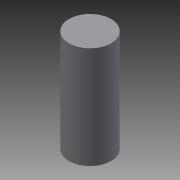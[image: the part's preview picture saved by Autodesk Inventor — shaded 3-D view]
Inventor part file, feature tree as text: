
AUTODESK INVENTOR PART (.ipt)
format: ipt  version: 2014 (Build 180170000, 170)  size: 81,920 bytes
history: native  units: mm
features: extrude x1, sketch x1
ambient origin geometry x8: Origin, YZ Plane, XZ Plane, XY Plane, X Axis, Y Axis, Z Axis, Center Point
bodies: Solid1 (feature_tree)
feature tree (2):
  extrude  "Extrusion1"  TaperAngle=0.0deg  [1 undecoded]
  sketch  "Sketch1"  dims[d2=0.0mm d3=0.0mm d4=0.0mm d9=0.0mm d10=0.0mm]
note: 1 required parameter value undecoded (feature->parameter linkage not recoverable at this tier; creation-order binding heuristic only, values carry confidence <= 0.55)
